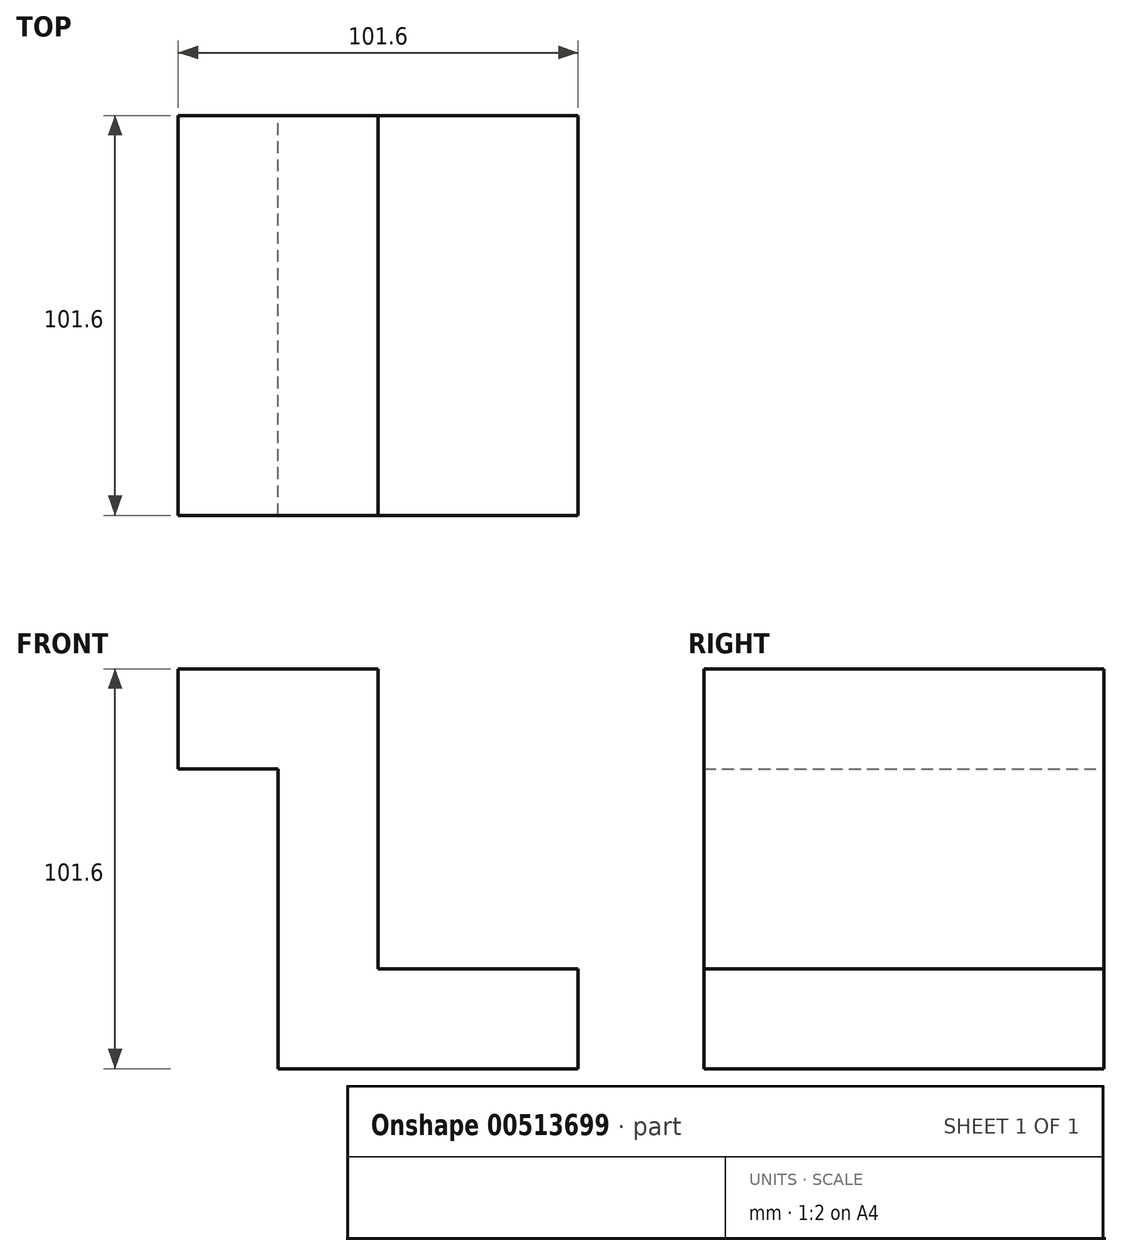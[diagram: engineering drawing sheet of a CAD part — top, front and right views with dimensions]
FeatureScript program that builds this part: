
annotation { "Feature Type Name" : "Feature", "Feature Type Description" : "" }
export const myFeature = defineFeature(function(context is Context, id is Id, definition is map)
    precondition{}
    {
        {
            var Q0;
            Q0=qCreatedBy(makeId("Front.planeOp"),FACE);
            var sketch = newSketch(context, id + "F0", { "sketchPlane" : qUnion([Q0])});
            skLineSegment(sketch, "E0", {"start": v(0, 0) * mm, "end": v(-76.2, 0) * mm});
            skLineSegment(sketch, "E1", {"start": v(-76.2, 0) * mm, "end": v(-76.2, 76.2) * mm});
            skLineSegment(sketch, "E2", {"start": v(-76.2, 76.2) * mm, "end": v(-101.6, 76.2) * mm});
            skLineSegment(sketch, "E3", {"start": v(-101.6, 76.2) * mm, "end": v(-101.6, 101.6) * mm});
            skLineSegment(sketch, "E4", {"start": v(-101.6, 101.6) * mm, "end": v(-50.8, 101.6) * mm});
            skLineSegment(sketch, "E5", {"start": v(-50.8, 101.6) * mm, "end": v(-50.8, 25.4) * mm});
            skLineSegment(sketch, "E6", {"start": v(-50.8, 25.4) * mm, "end": v(0, 25.4) * mm});
            skLineSegment(sketch, "E7", {"start": v(0, 25.4) * mm, "end": v(0, 0) * mm});
            skSolve(sketch);
        }
        {
            var Q0;
            Q0 = qSketchRegion(id + "F0", true);
            extrude(context, id + "F1", {"entities" : qUnion([Q0]), "depth" : 101.6 * mm});
        }
    });
